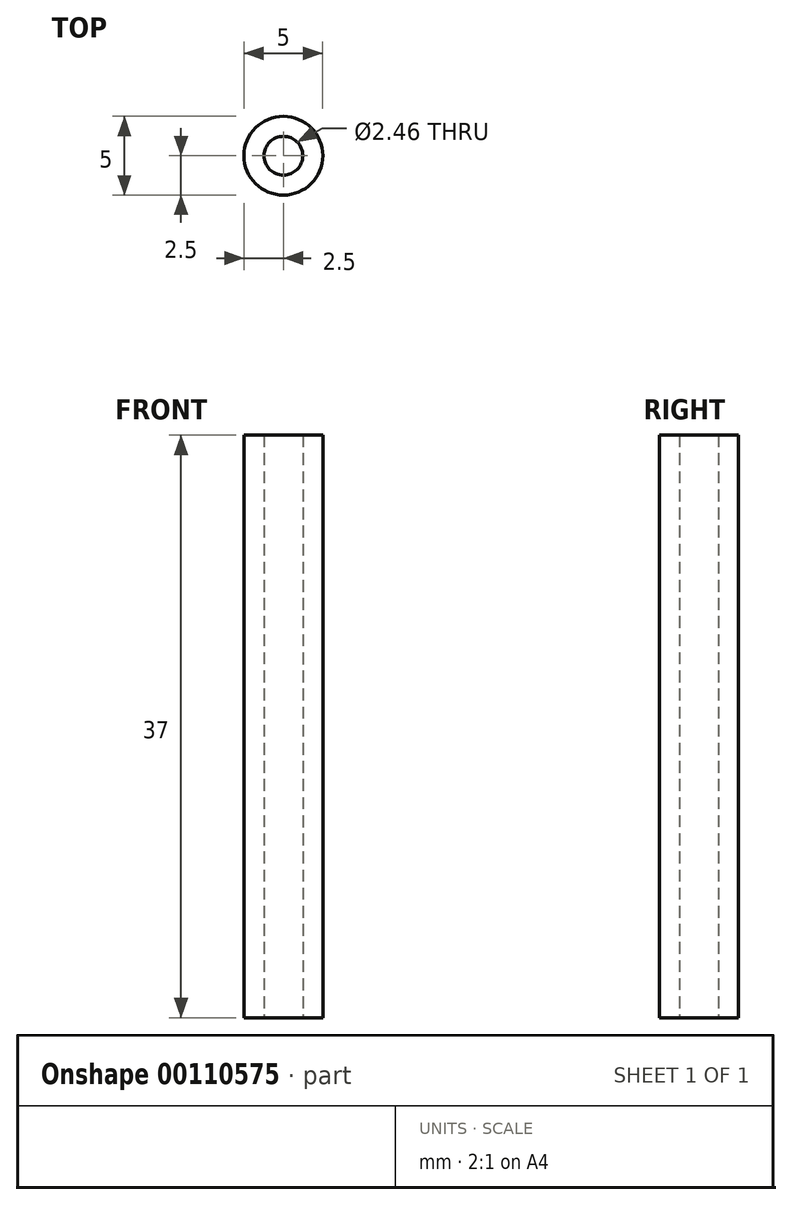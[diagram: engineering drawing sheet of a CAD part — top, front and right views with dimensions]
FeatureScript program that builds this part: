
annotation { "Feature Type Name" : "Feature", "Feature Type Description" : "" }
export const myFeature = defineFeature(function(context is Context, id is Id, definition is map)
    precondition{}
    {
        {
            var Q0;
            Q0=qCreatedBy(makeId("Top.planeOp"),FACE);
            var sketch = newSketch(context, id + "F0", { "sketchPlane" : qUnion([Q0])});
            skCircle(sketch, "E0", {"center": v(0, 0) * mm, "radius": 2.5 * mm});
            skCircle(sketch, "E1", {"center": v(0, 0) * mm, "radius": 1.23 * mm});
            skSolve(sketch);
        }
        {
            var Q0;
            Q0=makeQuery(id+"F0.imprint","IMPRINT",FACE,{"disambiguationData":[TD([[makeQuery(id+"F0.imprint","IMPRINT",EDGE,{"derivedFrom":sQuery(id+"F0.wireOp",EDGE,"E0")}),1.0]])]});
            extrude(context, id + "F1", {"entities" : qUnion([Q0]), "depth" : 37 * mm});
        }
    });
